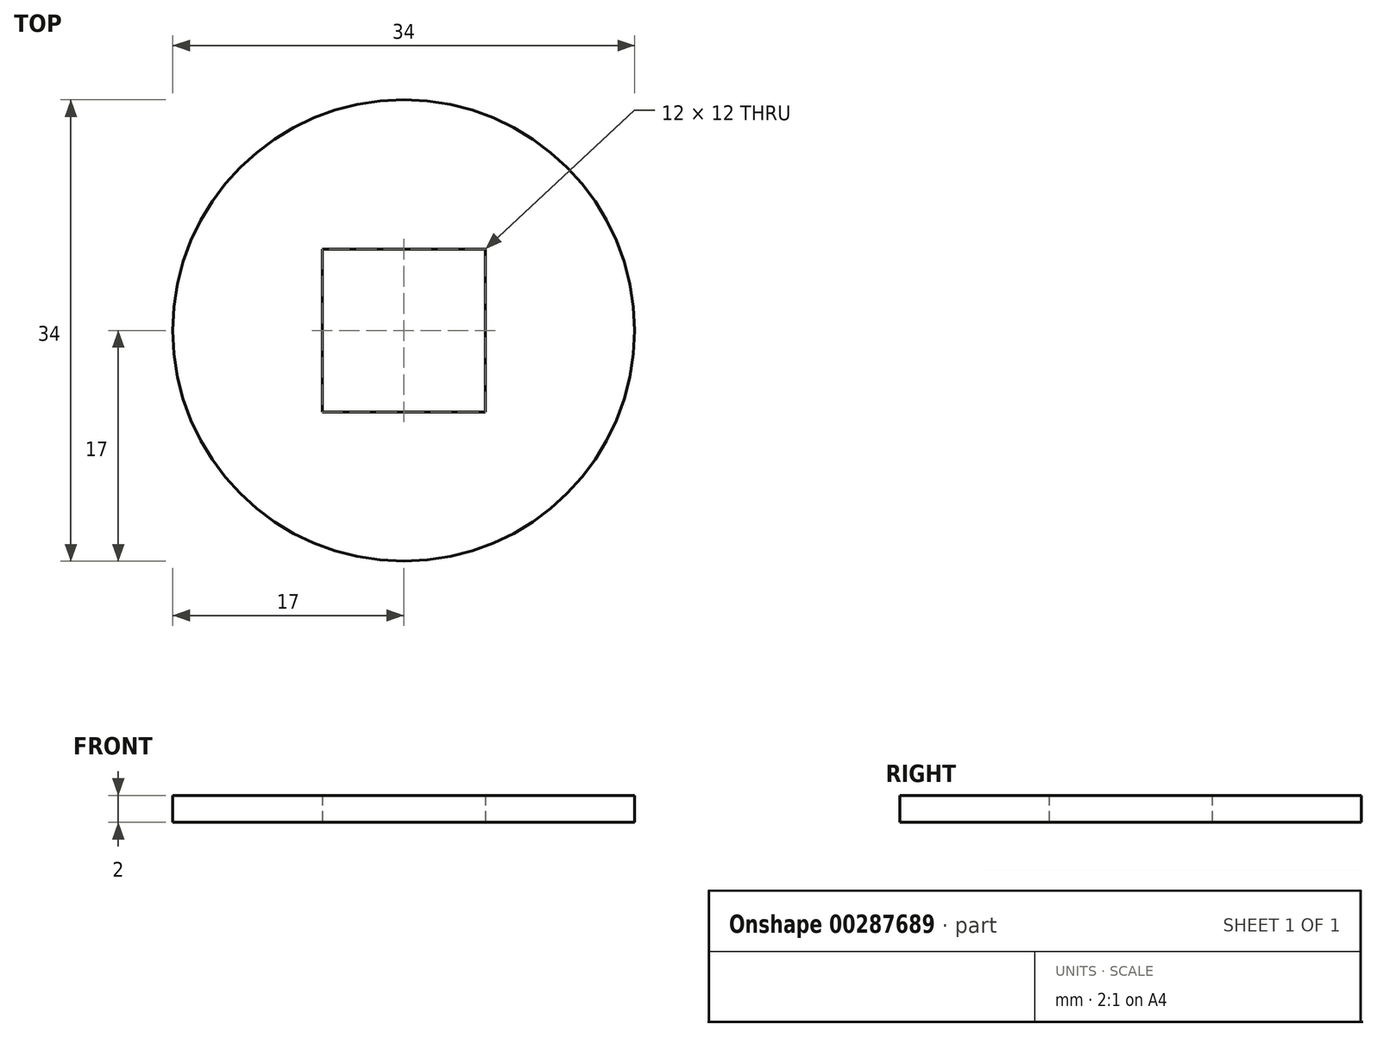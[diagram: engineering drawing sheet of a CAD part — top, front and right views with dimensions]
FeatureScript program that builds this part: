
annotation { "Feature Type Name" : "Feature", "Feature Type Description" : "" }
export const myFeature = defineFeature(function(context is Context, id is Id, definition is map)
    precondition{}
    {
        {
            var Q0;
            Q0=qCreatedBy(makeId("Top.planeOp"),FACE);
            var sketch = newSketch(context, id + "F0", { "sketchPlane" : qUnion([Q0])});
            skCircle(sketch, "E0", {"center": v(0, 0) * mm, "radius": 17 * mm});
            skLineSegment(sketch, "E1.bottom", {"start": v(6, 6) * mm, "end": v(-6, 6) * mm});
            skLineSegment(sketch, "E1.top", {"start": v(6, -6) * mm, "end": v(-6, -6) * mm});
            skLineSegment(sketch, "E1.left", {"start": v(6, 6) * mm, "end": v(6, -6) * mm});
            skLineSegment(sketch, "E1.right", {"start": v(-6, 6) * mm, "end": v(-6, -6) * mm});
            skSolve(sketch);
        }
        {
            var Q0;
            Q0 = qSketchRegion(id + "F0", true);
            extrude(context, id + "F1", {"entities" : qUnion([Q0]), "depth" : 2 * mm, "offsetDistance" : 25 * mm});
        }
    });
